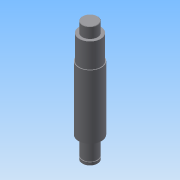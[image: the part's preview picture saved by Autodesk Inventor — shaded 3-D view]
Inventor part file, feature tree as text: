
AUTODESK INVENTOR PART (.ipt)
format: ipt  version: 2015 (Build 190159000, 159)  size: 131,584 bytes
history: native  units: mm
features: sketch x6, extrude x5, plane x1, chamfer x1, revolve x1
ambient origin geometry x8: Origin, YZ Plane, XZ Plane, XY Plane, X Axis, Y Axis, Z Axis, Center Point
bodies: 实体1 (feature_tree)
feature tree (14):
  extrude  "拉伸1"  Depth=28.378mm TaperAngle=0.0deg
  extrude  "拉伸2"  Depth=83.422mm TaperAngle=0.0deg
  extrude  "拉伸3"  Depth=32.0mm TaperAngle=0.0deg
  extrude  "拉伸4"  Depth=14.0mm TaperAngle=0.0deg
  plane  "工作平面1"
  extrude  "拉伸5"  Depth=6.0mm
  chamfer  "倒角1"  Distance=2.5mm
  revolve  "旋转1"  Angle=45.0deg
  sketch  "草图1"  dims[d0=20.0mm d1=28.378mm d2=0.0mm]
  sketch  "草图2"  dims[d3=30.0mm d4=83.422mm d5=0.0mm]
  sketch  "草图3"  dims[d6=28.0mm d7=32.0mm d8=0.0mm]
  sketch  "草图4"  dims[d9=20.0mm d10=14.0mm d11=0.0mm]
  sketch  "草图5"  dims[d12=4.728778mm d13=6.0mm]
  sketch  "草图6"  dims[d14=12.0mm d16=2.5mm d17=0.0mm d18=0.5mm d19=2.0mm d20=45.0deg d21=5.589mm d22=4.0mm d23=1.2mm d24=3.792368mm d25=9.175mm d26=5.235876mm d27=90.0deg]
